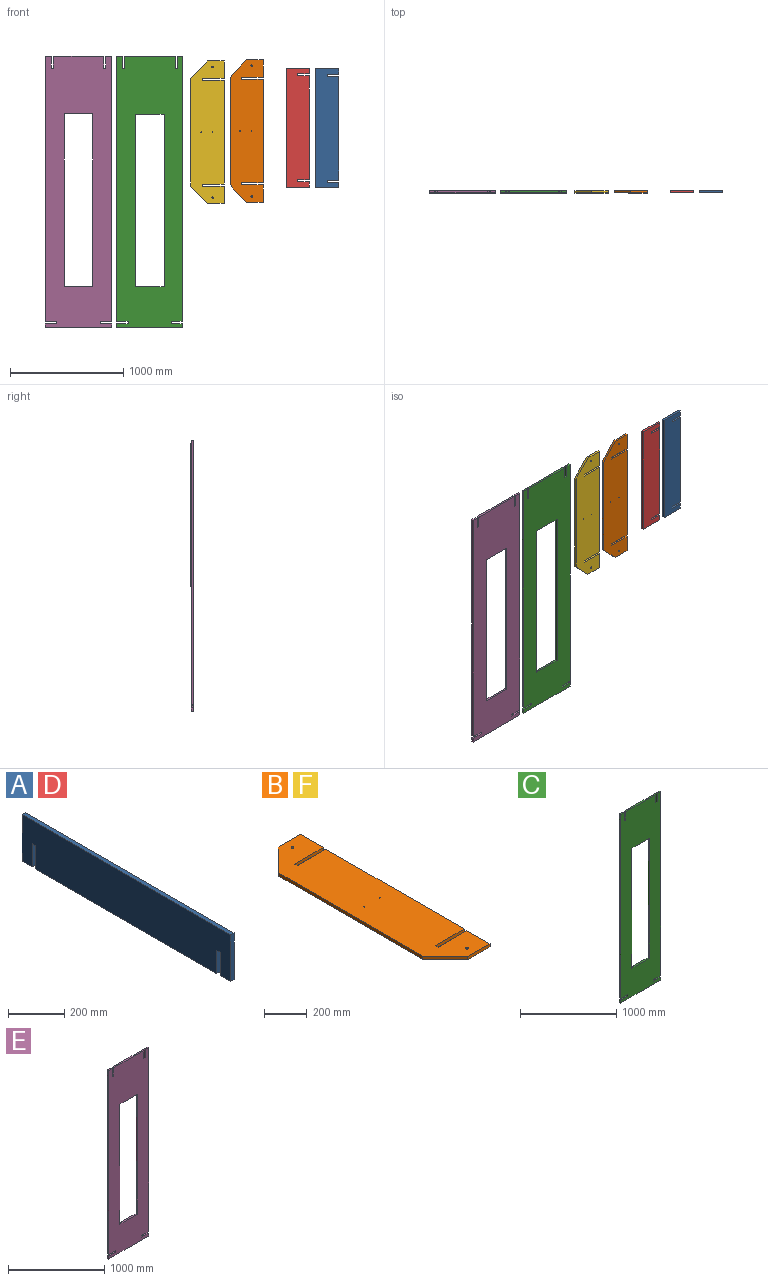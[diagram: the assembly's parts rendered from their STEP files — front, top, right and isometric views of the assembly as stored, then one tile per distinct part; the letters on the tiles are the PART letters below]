
ASSEMBLY  parts=6 mates=3
PART A: 14 faces, bbox 17.9x1051.7x203.2 mm
  f0: plane 101.6x17.86mm, normal (0,1,0), area 1814.2mm2, adj f1,f11,f12,f13
  f1: plane 17.86x17.86mm, normal (0,0,-1), area 318.8mm2, adj f0,f2,f12,f13
  f2: plane 101.6x17.86mm, normal (0,-1,0), area 1814.2mm2, adj f1,f3,f12,f13
  f3: plane 50.8x17.86mm, normal (0,0,-1), area 907.1mm2, adj f2,f4,f12,f13
  f4: plane 203.2x17.86mm, normal (0,1,0), area 3628.4mm2, adj f3,f5,f12,f13
  f5: plane 1051.71x17.86mm, normal (0,0,1), area 18779.6mm2, adj f4,f6,f12,f13
  f6: plane 203.2x17.86mm, normal (0,-1,0), area 3628.4mm2, adj f5,f7,f12,f13
  f7: plane 50.8x17.86mm, normal (0,0,-1), area 907.1mm2, adj f6,f8,f12,f13
  f8: plane 101.6x17.86mm, normal (0,1,0), area 1814.2mm2, adj f7,f9,f12,f13
  f9: plane 17.86x17.86mm, normal (0,0,-1), area 318.8mm2, adj f8,f10,f12,f13
  f10: plane 101.6x17.86mm, normal (0,-1,0), area 1814.2mm2, adj f9,f11,f12,f13
  f11: plane 914.4x17.86mm, normal (0,0,-1), area 16327.7mm2, adj f0,f10,f12,f13
  f12: plane 1051.71x203.2mm, normal (1,0,0), area 210079.6mm2, adj f0,f1,f2,f3,f4,f5,f6,f7
  f13: plane 1051.71x203.2mm, normal (-1,0,0), area 210079.6mm2, adj f0,f1,f2,f3,f4,f5,f6,f7
PART B: 20 faces, bbox 292.1x1254.9x17.9 mm
  f0: plane 146.05x17.86mm, normal (0,-1,0), area 2607.9mm2, adj f3,f4,f5,f16
  f1: plane 146.05x17.86mm, normal (0,1,0), area 2607.9mm2, adj f3,f4,f7,f15
  f2: plane 950.11x17.86mm, normal (-1,0,0), area 16965.4mm2, adj f3,f4,f15,f16
  f3: plane 1254.91x292.1mm, normal (0,0,1), area 337229.5mm2, adj f0,f1,f2,f5,f6,f7,f8,f9
  f4: plane 1254.91x292.1mm, normal (0,0,-1), area 337229.5mm2, adj f0,f1,f2,f5,f6,f7,f8,f9
  f5: plane 152.4x17.86mm, normal (1,0,0), area 2721.3mm2, adj f0,f3,f4,f12
  f6: plane 914.4x17.86mm, normal (1,0,0), area 16327.7mm2, adj f3,f4,f9,f11
  f7: plane 152.4x17.86mm, normal (1,0,0), area 2721.3mm2, adj f1,f3,f4,f8
  f8: plane 190.5x17.86mm, normal (0,-1,0), area 3401.6mm2, adj f3,f4,f7,f10
  f9: plane 190.5x17.86mm, normal (0,1,0), area 3401.6mm2, adj f3,f4,f6,f10
  f10: plane 17.86x17.86mm, normal (1,0,0), area 318.8mm2, adj f3,f4,f8,f9
  f11: plane 190.5x17.86mm, normal (0,-1,0), area 3401.6mm2, adj f3,f4,f6,f13
  f12: plane 190.5x17.86mm, normal (0,1,0), area 3401.6mm2, adj f3,f4,f5,f13
  f13: plane 17.86x17.86mm, normal (1,0,0), area 318.8mm2, adj f3,f4,f11,f12
  f14: cylinder r=6.35mm len=17.86mm, axis (0,0,1), area 712.4mm2, adj f3,f4
  f15: plane 152.4x146.05mm, normal (-0.72,0.69,0), area 3769.2mm2, adj f1,f2,f3,f4
  f16: plane 152.4x146.05mm, normal (-0.72,-0.69,0), area 3769.2mm2, adj f0,f2,f3,f4
  f17: cylinder r=1.59mm len=17.86mm, axis (0,0,1), area 178.1mm2, adj f3,f4
  f18: cylinder r=6.35mm len=17.86mm, axis (0,0,1), area 712.4mm2, adj f3,f4
  f19: cylinder r=1.59mm len=17.86mm, axis (0,0,1), area 178.1mm2, adj f3,f4
PART C: 34 faces, bbox 584.2x17.9x2392.8 mm
  f0: plane 31.75x17.86mm, normal (1,0,0), area 566.9mm2, adj f2,f5,f7,f31
  f1: plane 31.75x17.86mm, normal (-1,0,0), area 566.9mm2, adj f2,f5,f7,f33
  f2: plane 2392.76x584.2mm, normal (0,1,0), area 1003312.8mm2, adj f0,f1,f3,f4,f6,f7,f8,f9
  f3: plane 44.45x17.86mm, normal (0,0,1), area 793.7mm2, adj f2,f5,f8,f27
  f4: plane 44.45x17.86mm, normal (0,0,1), area 793.7mm2, adj f2,f5,f9,f28
  f5: plane 2392.76x584.2mm, normal (0,-1,0), area 1003312.8mm2, adj f0,f1,f3,f4,f6,f7,f8,f9
  f6: plane 434.19x17.86mm, normal (0,0,1), area 7752.9mm2, adj f2,f5,f26,f29
  f7: plane 584.2x17.86mm, normal (0,0,-1), area 10431.6mm2, adj f0,f1,f2,f5
  f8: plane 2330.45x17.86mm, normal (1,0,0), area 41613mm2, adj f2,f3,f5,f30
  f9: plane 2330.45x17.86mm, normal (-1,0,0), area 41613mm2, adj f2,f4,f5,f32
  f10: plane 254x17.86mm, normal (0,0,-1), area 4535.5mm2, adj f2,f5,f11,f13
  f11: plane 1524x17.86mm, normal (1,0,0), area 27212.8mm2, adj f2,f5,f10,f12
  f12: plane 254x17.86mm, normal (0,0,1), area 4535.5mm2, adj f2,f5,f11,f13
  f13: plane 1524x17.86mm, normal (-1,0,0), area 27212.8mm2, adj f2,f5,f10,f12
  f14: plane 95.25x17.86mm, normal (0,0,1), area 1700.8mm2, adj f2,f5,f15,f33
  f15: plane 17.86x17.86mm, normal (-1,0,0), area 318.8mm2, adj f2,f5,f14,f16
  f16: plane 95.25x17.86mm, normal (0,0,-1), area 1700.8mm2, adj f2,f5,f15,f32
  f17: plane 95.25x17.86mm, normal (0,0,1), area 1700.8mm2, adj f2,f5,f19,f31
  f18: plane 95.25x17.86mm, normal (0,0,-1), area 1700.8mm2, adj f2,f5,f19,f30
  f19: plane 17.86x17.86mm, normal (1,0,0), area 318.8mm2, adj f2,f5,f17,f18
  f20: plane 98.43x17.86mm, normal (1,0,0), area 1757.5mm2, adj f2,f5,f21,f28
  f21: plane 17.86x17.86mm, normal (0,0,1), area 318.8mm2, adj f2,f5,f20,f22
  f22: plane 98.43x17.86mm, normal (-1,0,0), area 1757.5mm2, adj f2,f5,f21,f29
  f23: plane 98.43x17.86mm, normal (1,0,0), area 1757.5mm2, adj f2,f5,f24,f26
  f24: plane 17.86x17.86mm, normal (0,0,1), area 318.8mm2, adj f2,f5,f23,f25
  f25: plane 98.43x17.86mm, normal (-1,0,0), area 1757.5mm2, adj f2,f5,f24,f27
  f26: cylinder r=6.35mm len=17.86mm, axis (0,1,0), area 178.1mm2, adj f2,f5,f6,f23
  f27: cylinder r=6.35mm len=17.86mm, axis (0,-1,0), area 178.1mm2, adj f2,f3,f5,f25
  f28: cylinder r=6.35mm len=17.86mm, axis (0,1,0), area 178.1mm2, adj f2,f4,f5,f20
  f29: cylinder r=6.35mm len=17.86mm, axis (0,-1,0), area 178.1mm2, adj f2,f5,f6,f22
  f30: cylinder r=6.35mm len=17.86mm, axis (0,1,0), area 178.1mm2, adj f2,f5,f8,f18
  f31: cylinder r=6.35mm len=17.86mm, axis (0,-1,0), area 178.1mm2, adj f0,f2,f5,f17
  f32: cylinder r=6.35mm len=17.86mm, axis (0,-1,0), area 178.1mm2, adj f2,f5,f9,f16
  f33: cylinder r=6.35mm len=17.86mm, axis (0,1,0), area 178.1mm2, adj f1,f2,f5,f14
PART D: same geometry as A
PART E: 34 faces, bbox 584.2x17.9x2392.8 mm
  f0: plane 31.75x17.86mm, normal (1,0,0), area 566.9mm2, adj f2,f5,f6,f31
  f1: plane 31.75x17.86mm, normal (-1,0,0), area 566.9mm2, adj f2,f5,f6,f33
  f2: plane 2392.76x584.2mm, normal (0,1,0), area 1003312.8mm2, adj f0,f1,f3,f4,f6,f7,f8,f9
  f3: plane 44.45x17.86mm, normal (0,0,1), area 793.7mm2, adj f2,f5,f8,f27
  f4: plane 44.45x17.86mm, normal (0,0,1), area 793.7mm2, adj f2,f5,f9,f28
  f5: plane 2392.76x584.2mm, normal (0,-1,0), area 1003312.8mm2, adj f0,f1,f3,f4,f6,f7,f8,f9
  f6: plane 584.2x17.86mm, normal (0,0,-1), area 10431.6mm2, adj f0,f1,f2,f5
  f7: plane 434.19x17.86mm, normal (0,0,1), area 7752.9mm2, adj f2,f5,f26,f29
  f8: plane 2330.45x17.86mm, normal (1,0,0), area 41613mm2, adj f2,f3,f5,f30
  f9: plane 2330.45x17.86mm, normal (-1,0,0), area 41613mm2, adj f2,f4,f5,f32
  f10: plane 254x17.86mm, normal (0,0,-1), area 4535.5mm2, adj f2,f5,f11,f13
  f11: plane 1524x17.86mm, normal (1,0,0), area 27212.8mm2, adj f2,f5,f10,f12
  f12: plane 254x17.86mm, normal (0,0,1), area 4535.5mm2, adj f2,f5,f11,f13
  f13: plane 1524x17.86mm, normal (-1,0,0), area 27212.8mm2, adj f2,f5,f10,f12
  f14: plane 95.25x17.86mm, normal (0,0,1), area 1700.8mm2, adj f2,f5,f15,f33
  f15: plane 17.86x17.86mm, normal (-1,0,0), area 318.8mm2, adj f2,f5,f14,f16
  f16: plane 95.25x17.86mm, normal (0,0,-1), area 1700.8mm2, adj f2,f5,f15,f32
  f17: plane 95.25x17.86mm, normal (0,0,1), area 1700.8mm2, adj f2,f5,f19,f31
  f18: plane 95.25x17.86mm, normal (0,0,-1), area 1700.8mm2, adj f2,f5,f19,f30
  f19: plane 17.86x17.86mm, normal (1,0,0), area 318.8mm2, adj f2,f5,f17,f18
  f20: plane 17.86x17.86mm, normal (0,0,1), area 318.8mm2, adj f2,f5,f21,f22
  f21: plane 98.43x17.86mm, normal (1,0,0), area 1757.5mm2, adj f2,f5,f20,f28
  f22: plane 98.43x17.86mm, normal (-1,0,0), area 1757.5mm2, adj f2,f5,f20,f29
  f23: plane 17.86x17.86mm, normal (0,0,1), area 318.8mm2, adj f2,f5,f24,f25
  f24: plane 98.43x17.86mm, normal (1,0,0), area 1757.5mm2, adj f2,f5,f23,f26
  f25: plane 98.43x17.86mm, normal (-1,0,0), area 1757.5mm2, adj f2,f5,f23,f27
  f26: cylinder r=6.35mm len=17.86mm, axis (0,1,0), area 178.1mm2, adj f2,f5,f7,f24
  f27: cylinder r=6.35mm len=17.86mm, axis (0,-1,0), area 178.1mm2, adj f2,f3,f5,f25
  f28: cylinder r=6.35mm len=17.86mm, axis (0,1,0), area 178.1mm2, adj f2,f4,f5,f21
  f29: cylinder r=6.35mm len=17.86mm, axis (0,-1,0), area 178.1mm2, adj f2,f5,f7,f22
  f30: cylinder r=6.35mm len=17.86mm, axis (0,1,0), area 178.1mm2, adj f2,f5,f8,f18
  f31: cylinder r=6.35mm len=17.86mm, axis (0,-1,0), area 178.1mm2, adj f0,f2,f5,f17
  f32: cylinder r=6.35mm len=17.86mm, axis (0,-1,0), area 178.1mm2, adj f2,f5,f9,f16
  f33: cylinder r=6.35mm len=17.86mm, axis (0,1,0), area 178.1mm2, adj f1,f2,f5,f14
PART F: same geometry as B
PLACE A rot(axis=(0.58,-0.58,-0.58),120deg) t=(2302.86,59.73,584.24)mm
PLACE B rot(axis=(1,0,0),90deg) t=(278.88,-1076.3,559.1)mm
PLACE C t=(-721.8,464.73,-53.17)mm
PLACE D rot(axis=(0.58,-0.58,-0.58),120deg) t=(2043.61,59.15,588.26)mm
PLACE E t=(-1349.29,-467.52,-50.46)mm
PLACE F rot(axis=(1,0,0),90deg) t=(-65.58,-1077.12,549.54)mm
MATE planar F.f3 <-> C.f5  axis (0,-1,0) through (85.84,-10.32,549.54)mm
MATE planar D.f12 <-> B.f3  axis (0,-1,0) through (875.21,-9.5,1054.38)mm
MATE planar E.f5 <-> C.f5  axis (0,-1,0) through (-824.82,-10.32,1114.76)mm
